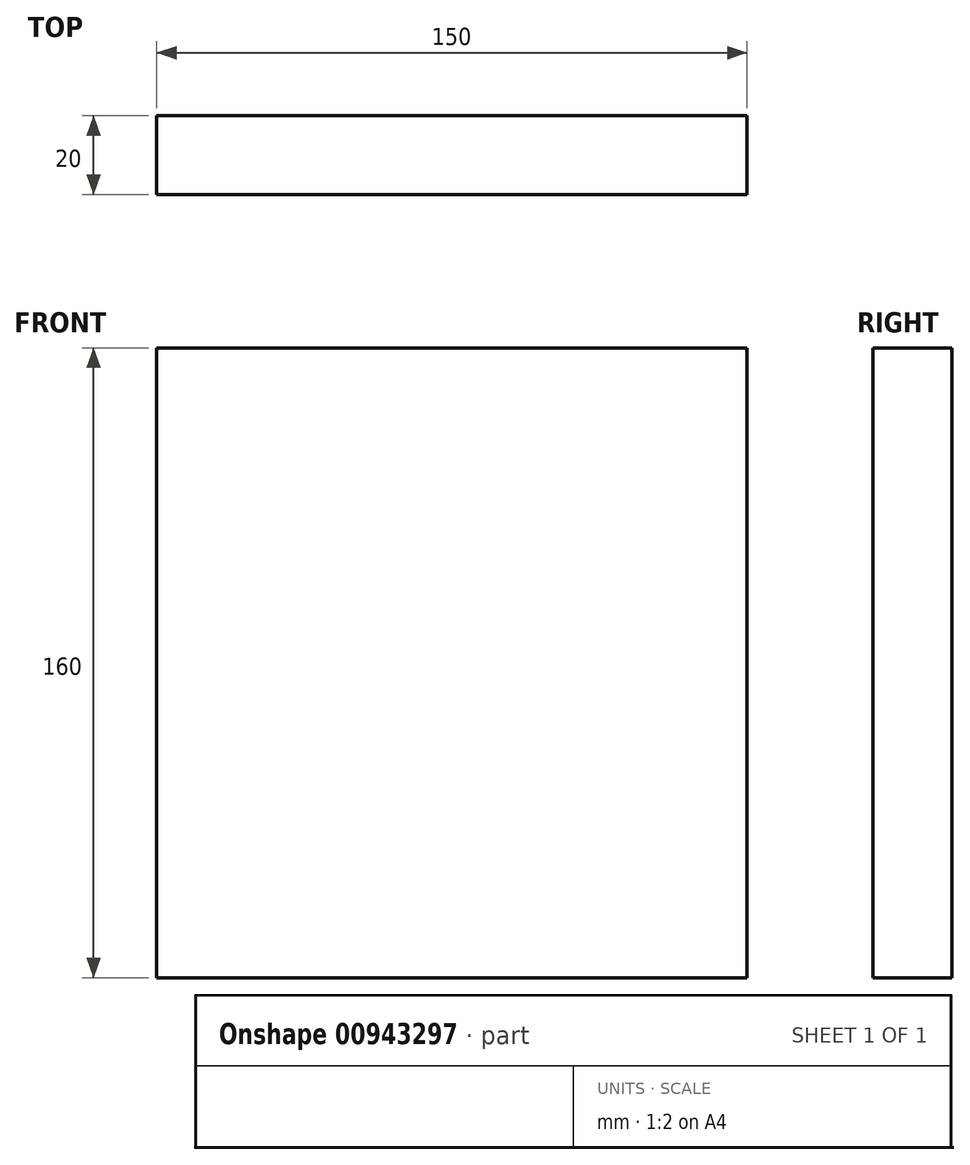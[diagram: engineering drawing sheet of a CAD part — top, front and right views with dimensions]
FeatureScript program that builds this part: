
annotation { "Feature Type Name" : "Feature", "Feature Type Description" : "" }
export const myFeature = defineFeature(function(context is Context, id is Id, definition is map)
    precondition{}
    {
        {
            var Q0;
            Q0=qCreatedBy(makeId("Front.planeOp"),FACE);
            var sketch = newSketch(context, id + "F0", { "sketchPlane" : qUnion([Q0])});
            skLineSegment(sketch, "E0.bottom", {"start": v(0, 0) * mm, "end": v(150, 0) * mm});
            skLineSegment(sketch, "E0.top", {"start": v(0, 160) * mm, "end": v(150, 160) * mm});
            skLineSegment(sketch, "E0.left", {"start": v(0, 0) * mm, "end": v(0, 160) * mm});
            skLineSegment(sketch, "E0.right", {"start": v(150, 0) * mm, "end": v(150, 160) * mm});
            skSolve(sketch);
        }
        {
            var Q0;
            Q0 = qSketchRegion(id + "F0", true);
            extrude(context, id + "F1", {"entities" : qUnion([Q0]), "depth" : 20 * mm, "offsetDistance" : 25 * mm});
        }
    });
